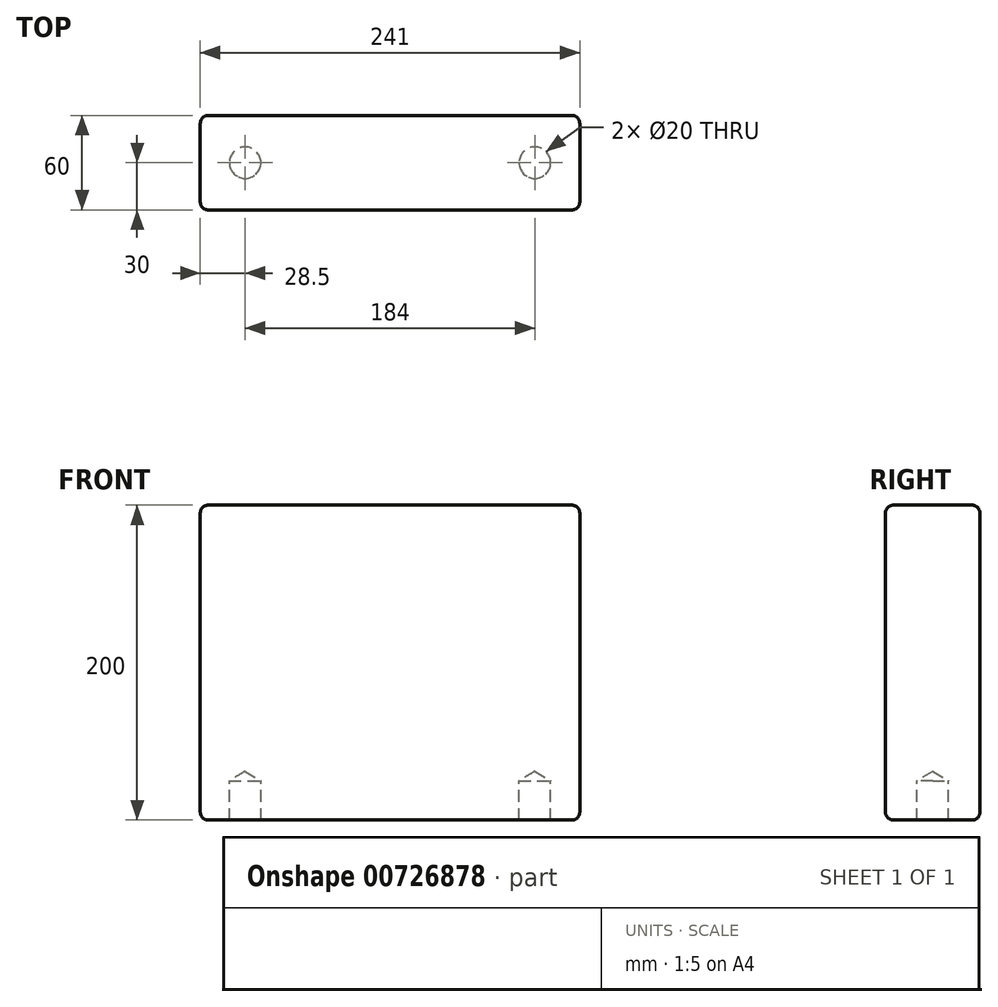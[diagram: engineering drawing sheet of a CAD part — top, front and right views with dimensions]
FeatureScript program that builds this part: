
annotation { "Feature Type Name" : "Feature", "Feature Type Description" : "" }
export const myFeature = defineFeature(function(context is Context, id is Id, definition is map)
    precondition{}
    {
        {
            var Q0;
            Q0=qCreatedBy(makeId("Front.planeOp"),FACE);
            var sketch = newSketch(context, id + "F0", { "sketchPlane" : qUnion([Q0])});
            skLineSegment(sketch, "E0", {"start": v(0, 0) * mm, "end": v(0, 200) * mm});
            skLineSegment(sketch, "E1", {"start": v(0, 200) * mm, "end": v(241, 200) * mm});
            skLineSegment(sketch, "E2", {"start": v(241, 200) * mm, "end": v(241, 0) * mm});
            skLineSegment(sketch, "E3", {"start": v(241, 0) * mm, "end": v(0, 0) * mm});
            skSolve(sketch);
        }
        {
            var Q0;
            Q0 = qSketchRegion(id + "F0", true);
            extrude(context, id + "F1", {"entities" : qUnion([Q0]), "depth" : 60 * mm, "offsetDistance" : 25 * mm});
        }
        {
            var Q0;
            Q0=qCreatedBy(makeId("Top.planeOp"),FACE);
            var sketch = newSketch(context, id + "F2", { "sketchPlane" : qUnion([Q0])});
            skLineSegment(sketch, "E4", {"start": v(0, 0) * mm, "end": v(0, -30) * mm});
            skLineSegment(sketch, "E5", {"start": v(0, -30) * mm, "end": v(28.5, -30) * mm});
            skLineSegment(sketch, "E6", {"start": v(28.5, -30) * mm, "end": v(212.5, -30) * mm});
            skLineSegment(sketch, "E7", {"start": v(212.5, -30) * mm, "end": v(241, -30) * mm});
            skPoint(sketch, "E8", {"position": v(28.5, -30) * mm});
            skPoint(sketch, "E9", {"position": v(212.5, -30) * mm});
            skSolve(sketch);
        }
        {
            var Q0;
            Q0=sQuery(id+"F2.wireOp",VERTEX,"E8");
            var Q1;
            Q1=sQuery(id+"F2.wireOp",VERTEX,"E9");
            var Q2;
            Q2=makeQuery(id+"F1.opExtrude","SWEPT_BODY",BODY,{"disambiguationData":[OSD([sQuery(id+"F0.wireOp",EDGE,"E0"),sQuery(id+"F0.wireOp",EDGE,"E1"),sQuery(id+"F0.wireOp",EDGE,"E2"),sQuery(id+"F0.wireOp",EDGE,"E3")])]});
            hole(context, id + "F3", {"style" : HoleStyle.SIMPLE, "endStyle" : HoleEndStyle.BLIND, "oppositeDirection" : true, "holeDiameter" : 20 * mm, "majorDiameter" : 20 * mm, "holeDepth" : 25 * mm, "isTappedThrough" : true, "tappedDepth" : 12 * mm, "tapClearance" : 3, "locations" : qUnion([Q0, Q1]), "scope" : qUnion([Q2])});
        }
        {
            var Q0;
            Q0=makeQuery(id+"F1.opExtrude","CAP_EDGE",EDGE,{"disambiguationData":[OSD([sQuery(id+"F0.wireOp",EDGE,"E1")])],"isStart":false});
            var Q1;
            Q1=makeQuery(id+"F1.opExtrude","CAP_EDGE",EDGE,{"disambiguationData":[OSD([sQuery(id+"F0.wireOp",EDGE,"E2")])],"isStart":false});
            var Q2;
            Q2=makeQuery(id+"F1.opExtrude","SWEPT_EDGE",EDGE,{"disambiguationData":[OSD([sQuery(id+"F0.wireOp",EDGE,"E1"),sQuery(id+"F0.wireOp",EDGE,"E2")])]});
            var Q3;
            Q3=makeQuery(id+"F1.opExtrude","CAP_EDGE",EDGE,{"disambiguationData":[OSD([sQuery(id+"F0.wireOp",EDGE,"E2")])],"isStart":true});
            var Q4;
            Q4=makeQuery(id+"F1.opExtrude","SWEPT_EDGE",EDGE,{"disambiguationData":[OSD([sQuery(id+"F0.wireOp",EDGE,"E2"),sQuery(id+"F0.wireOp",EDGE,"E3")])]});
            var Q5;
            Q5=makeQuery(id+"F1.opExtrude","CAP_EDGE",EDGE,{"disambiguationData":[OSD([sQuery(id+"F0.wireOp",EDGE,"E3")])],"isStart":false});
            var Q6;
            Q6=makeQuery(id+"F1.opExtrude","CAP_EDGE",EDGE,{"disambiguationData":[OSD([sQuery(id+"F0.wireOp",EDGE,"E0")])],"isStart":false});
            var Q7;
            Q7=makeQuery(id+"F1.opExtrude","SWEPT_EDGE",EDGE,{"disambiguationData":[OSD([sQuery(id+"F0.wireOp",EDGE,"E0"),sQuery(id+"F0.wireOp",EDGE,"E1")])]});
            var Q8;
            Q8=makeQuery(id+"F1.opExtrude","CAP_EDGE",EDGE,{"disambiguationData":[OSD([sQuery(id+"F0.wireOp",EDGE,"E1")])],"isStart":true});
            var Q9;
            Q9=makeQuery(id+"F1.opExtrude","CAP_EDGE",EDGE,{"disambiguationData":[OSD([sQuery(id+"F0.wireOp",EDGE,"E0")])],"isStart":true});
            var Q10;
            Q10=makeQuery(id+"F1.opExtrude","SWEPT_EDGE",EDGE,{"disambiguationData":[OSD([sQuery(id+"F0.wireOp",EDGE,"E0"),sQuery(id+"F0.wireOp",EDGE,"E3")])]});
            var Q11;
            Q11=makeQuery(id+"F1.opExtrude","CAP_EDGE",EDGE,{"disambiguationData":[OSD([sQuery(id+"F0.wireOp",EDGE,"E3")])],"isStart":true});
            fillet(context, id + "F4", {"entities" : qUnion([Q0, Q1, Q2, Q3, Q4, Q5, Q6, Q7, Q8, Q9, Q10, Q11]), "radius" : 5 * mm, "tangentPropagation" : true, "allowEdgeOverflow" : false});
        }
    });
